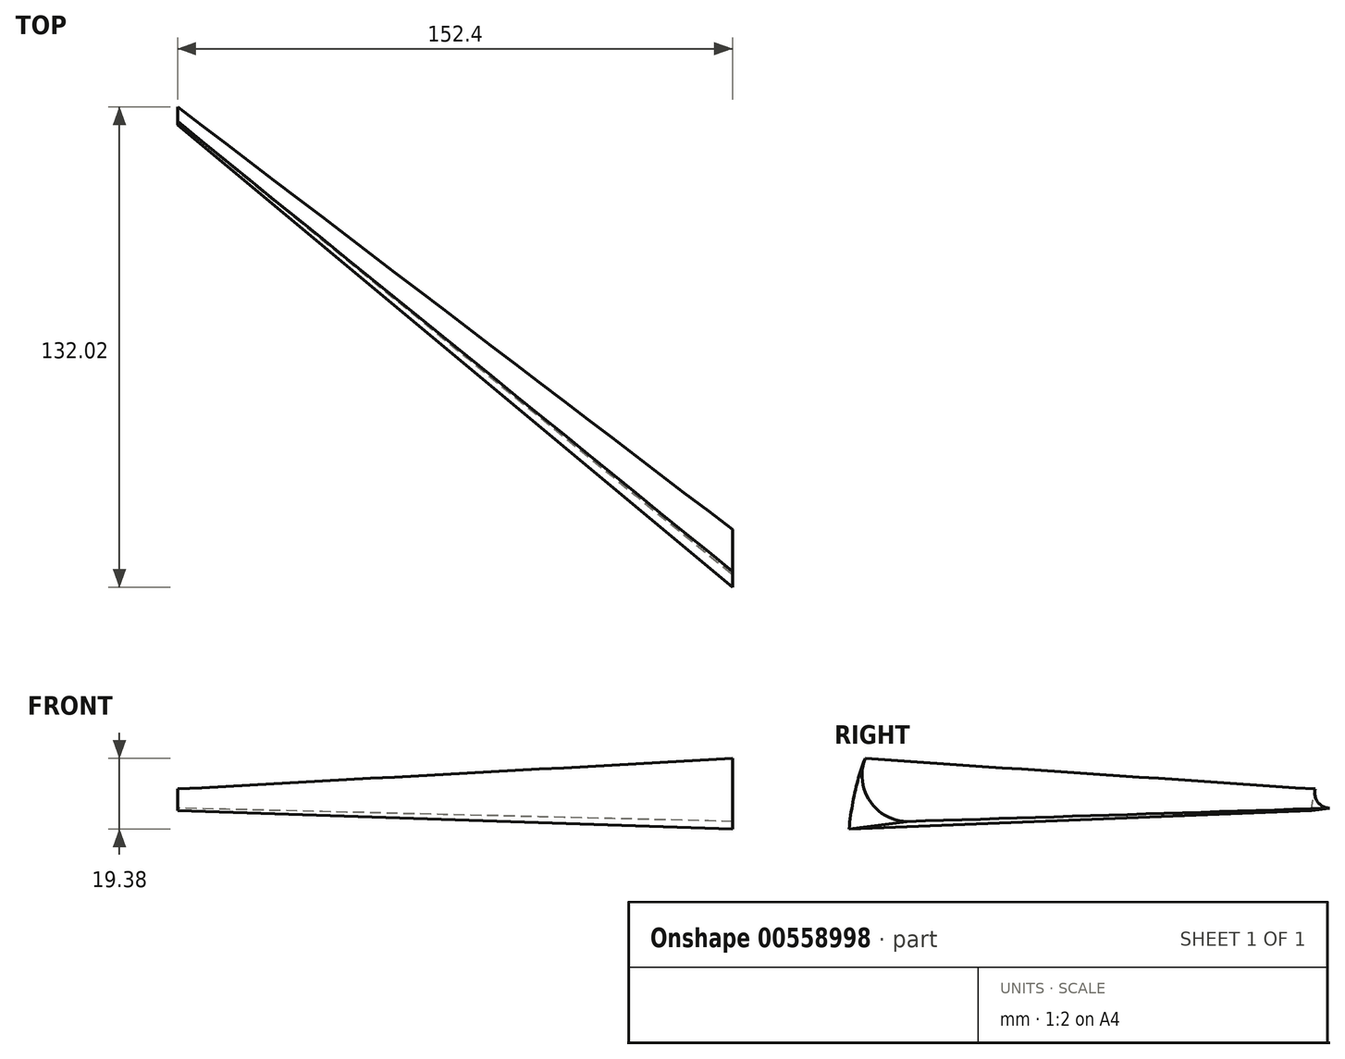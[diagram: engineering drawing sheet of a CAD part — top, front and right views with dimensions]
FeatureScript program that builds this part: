
annotation { "Feature Type Name" : "Feature", "Feature Type Description" : "" }
export const myFeature = defineFeature(function(context is Context, id is Id, definition is map)
    precondition{}
    {
        {
            var Q0;
            Q0=qCreatedBy(makeId("Right.planeOp"),FACE);
            cPlane(context, id + "F0", {"entities" : qUnion([Q0]), "cplaneType" : CPlaneType.OFFSET, "offset" : 25.4 * mm, "width" : 152.4 * mm, "height" : 152.4 * mm});
        }
        {
            var Q0;
            Q0=qCreatedBy(id+"F0.planeOp",FACE);
            var sketch = newSketch(context, id + "F1", { "sketchPlane" : qUnion([Q0])});
            skPoint(sketch, "E0", {"position": v(0, 0) * mm});
            skPoint(sketch, "E1", {"position": v(355.6, 0) * mm});
            skPoint(sketch, "E2", {"position": v(254, 5.55) * mm});
            skPoint(sketch, "E3", {"position": v(254, 25.4) * mm});
            skPoint(sketch, "E4", {"position": v(50.8, 50.8) * mm});
            skFitSpline(sketch, "E5", {"points": [v(0, 0) * mm, v(50.8, 50.8) * mm, v(254, 25.4) * mm, v(355.6, 0) * mm, v(254, 5.55) * mm], "startDerivative": vector(54.3, 516.72) * mm, "endDerivative": vector(-643.37, 57.95) * mm});
            skFitSpline(sketch, "E6", {"points": [v(254, 5.55) * mm, v(0, 0) * mm], "startDerivative": vector(-151.2, 19.05) * mm, "endDerivative": vector(-291.33, -38.1) * mm});
            skLineSegment(sketch, "E7", {"start": v(3.56, 33.87) * mm, "end": v(0, 0) * mm});
            skLineSegment(sketch, "E8", {"start": v(0, 0) * mm, "end": v(0, 76.62) * mm});
            skLineSegment(sketch, "E9", {"start": v(97.11, 12.7) * mm, "end": v(0, 0) * mm});
            skArc(sketch, "E10.filletArc", {"start": v(4.42, 19.38) * mm, "mid": v(6.2, 7.03) * mm, "end": v(17.68, 2.16) * mm});
            skLineSegment(sketch, "E11", {"start": v(203.6, 11.9) * mm, "end": v(254, 5.55) * mm});
            skSolve(sketch);
        }
        {
            var Q0;
            Q0=qCreatedBy(makeId("Right.planeOp"),FACE);
            cPlane(context, id + "F2", {"entities" : qUnion([Q0]), "cplaneType" : CPlaneType.OFFSET, "offset" : 177.8 * mm, "width" : 152.4 * mm, "height" : 152.4 * mm});
        }
        {
            var Q0;
            Q0=qCreatedBy(id+"F2.planeOp",FACE);
            var sketch = newSketch(context, id + "F3", { "sketchPlane" : qUnion([Q0])});
            skPoint(sketch, "E12", {"position": v(127, 5.08) * mm});
            skPoint(sketch, "E13", {"position": v(152.4, 30.48) * mm});
            skPoint(sketch, "E14", {"position": v(254, 17.78) * mm});
            skPoint(sketch, "E15", {"position": v(304.8, 5.08) * mm});
            skPoint(sketch, "E16", {"position": v(254, 11.43) * mm});
            skFitSpline(sketch, "E17", {"points": [v(127, 5.08) * mm, v(152.4, 30.48) * mm, v(254, 17.78) * mm, v(304.8, 5.08) * mm, v(254, 11.43) * mm], "startDerivative": vector(27.17, 258.55) * mm, "endDerivative": vector(-321.25, 46.07) * mm});
            skFitSpline(sketch, "E18", {"points": [v(254, 11.43) * mm, v(127, 5.08) * mm], "startDerivative": vector(-50.4, 6.35) * mm, "endDerivative": vector(-97.11, -12.7) * mm});
            skLineSegment(sketch, "E19", {"start": v(127, 5.08) * mm, "end": v(127, 20) * mm});
            skLineSegment(sketch, "E20", {"start": v(128.78, 22.01) * mm, "end": v(127, 5.08) * mm});
            skLineSegment(sketch, "E21", {"start": v(127, 5.08) * mm, "end": v(159.37, 9.31) * mm});
            skLineSegment(sketch, "E22", {"start": v(254, 11.43) * mm, "end": v(254, 15.33) * mm});
            skLineSegment(sketch, "E23", {"start": v(237.2, 13.55) * mm, "end": v(254, 11.43) * mm});
            skArc(sketch, "E24.filletArc", {"start": v(128.02, 11) * mm, "mid": v(128.94, 7.18) * mm, "end": v(132.6, 5.76) * mm});
            skSolve(sketch);
        }
        {
            var Q0;
            {var subQ0=sQuery(id+"F1.wireOp",EDGE,"E5");Q0=makeQuery(id+"F1.imprint","IMPRINT",FACE,{"disambiguationData":[TD([[makeQuery(id+"F1.imprint","IMPRINT",EDGE,{"derivedFrom":subQ0}),-1.0]])]});}
            var Q1;
            {var subQ0=sQuery(id+"F3.wireOp",EDGE,"E17");Q1=makeQuery(id+"F3.imprint","IMPRINT",FACE,{"disambiguationData":[TD([[makeQuery(id+"F3.imprint","IMPRINT",EDGE,{"derivedFrom":subQ0}),-1.0]])]});}
            loft(context, id + "F4", {"sheetProfilesArray" : [{ "sheetProfileEntities" : qUnion([Q0]) }, { "sheetProfileEntities" : qUnion([Q1]) }]});
        }
        {
            var Q0;
            {var subQ0=sQuery(id+"F1.wireOp",EDGE,"E5");Q0=makeQuery(id+"F4.opLoft","CAP_FACE",FACE,{"disambiguationData":[OSD([makeQuery(id+"F1.imprint","IMPRINT",FACE,{"disambiguationData":[TD([[makeQuery(id+"F1.imprint","IMPRINT",EDGE,{"derivedFrom":subQ0}),-1.0]])]})])],"isStart":true});}
            var sketch = newSketch(context, id + "F5", { "sketchPlane" : qUnion([Q0])});
            skPoint(sketch, "E25", {"position": v(-47.62, 27.02) * mm});
            skCircle(sketch, "E26", {"center": v(-47.62, 27.02) * mm, "radius": 12.7 * mm});
            skSolve(sketch);
        }
        {
            var Q0;
            Q0=makeQuery(id+"F5.imprint","IMPRINT",FACE,{"disambiguationData":[TD([[makeQuery(id+"F5.imprint","IMPRINT",EDGE,{"derivedFrom":sQuery(id+"F5.wireOp",EDGE,"E26")}),1.0]])]});
            extrude(context, id + "F6", {"entities" : qUnion([Q0]), "operationType" : NewBodyOperationType.ADD, "depth" : 25.4 * mm, "offsetDistance" : 25.4 * mm});
        }
        {
            var Q0;
            {var subQ0=sQuery(id+"F3.wireOp",EDGE,"E17");var subQ3=sQuery(id+"F1.wireOp",EDGE,"E5");Q0=makeQuery(id+"F4.opLoft","SWEPT_BODY",BODY,{"disambiguationData":[OSD([makeQuery(id+"F1.imprint","IMPRINT",FACE,{"disambiguationData":[TD([[makeQuery(id+"F1.imprint","IMPRINT",EDGE,{"derivedFrom":subQ3}),-1.0]])]}),makeQuery(id+"F3.imprint","IMPRINT",FACE,{"disambiguationData":[TD([[makeQuery(id+"F3.imprint","IMPRINT",EDGE,{"derivedFrom":subQ0}),-1.0]])]})])]});}
            var Q1;
            Q1=qCreatedBy(makeId("Right.planeOp"),FACE);
            mirror(context, id + "F7", {"operationType" : NewBodyOperationType.ADD, "entities" : qUnion([Q0]), "mirrorPlane" : qUnion([Q1])});
        }
        {
            var Q0;
            Q0=qCreatedBy(makeId("Top.planeOp"),FACE);
            var sketch = newSketch(context, id + "F8", { "sketchPlane" : qUnion([Q0])});
            skLineSegment(sketch, "E27.bottom", {"start": v(0, 0) * mm, "end": v(274.97, 0) * mm});
            skLineSegment(sketch, "E27.top", {"start": v(0, 420.7) * mm, "end": v(274.97, 420.7) * mm});
            skLineSegment(sketch, "E27.left", {"start": v(0, 0) * mm, "end": v(0, 420.7) * mm});
            skLineSegment(sketch, "E27.right", {"start": v(274.97, 0) * mm, "end": v(274.97, 420.7) * mm});
            skSolve(sketch);
        }
        {
            var Q0;
            Q0=makeQuery(id+"F8.imprint","IMPRINT",FACE,{"disambiguationData":[TD([[makeQuery(id+"F8.imprint","IMPRINT",EDGE,{"derivedFrom":sQuery(id+"F8.wireOp",EDGE,"E27.bottom")}),1.0]])]});
            extrude(context, id + "F9", {"entities" : qUnion([Q0]), "operationType" : NewBodyOperationType.REMOVE, "endBound" : BoundingType.SYMMETRIC, "depth" : 254 * mm, "offsetDistance" : 25.4 * mm});
        }
    });
